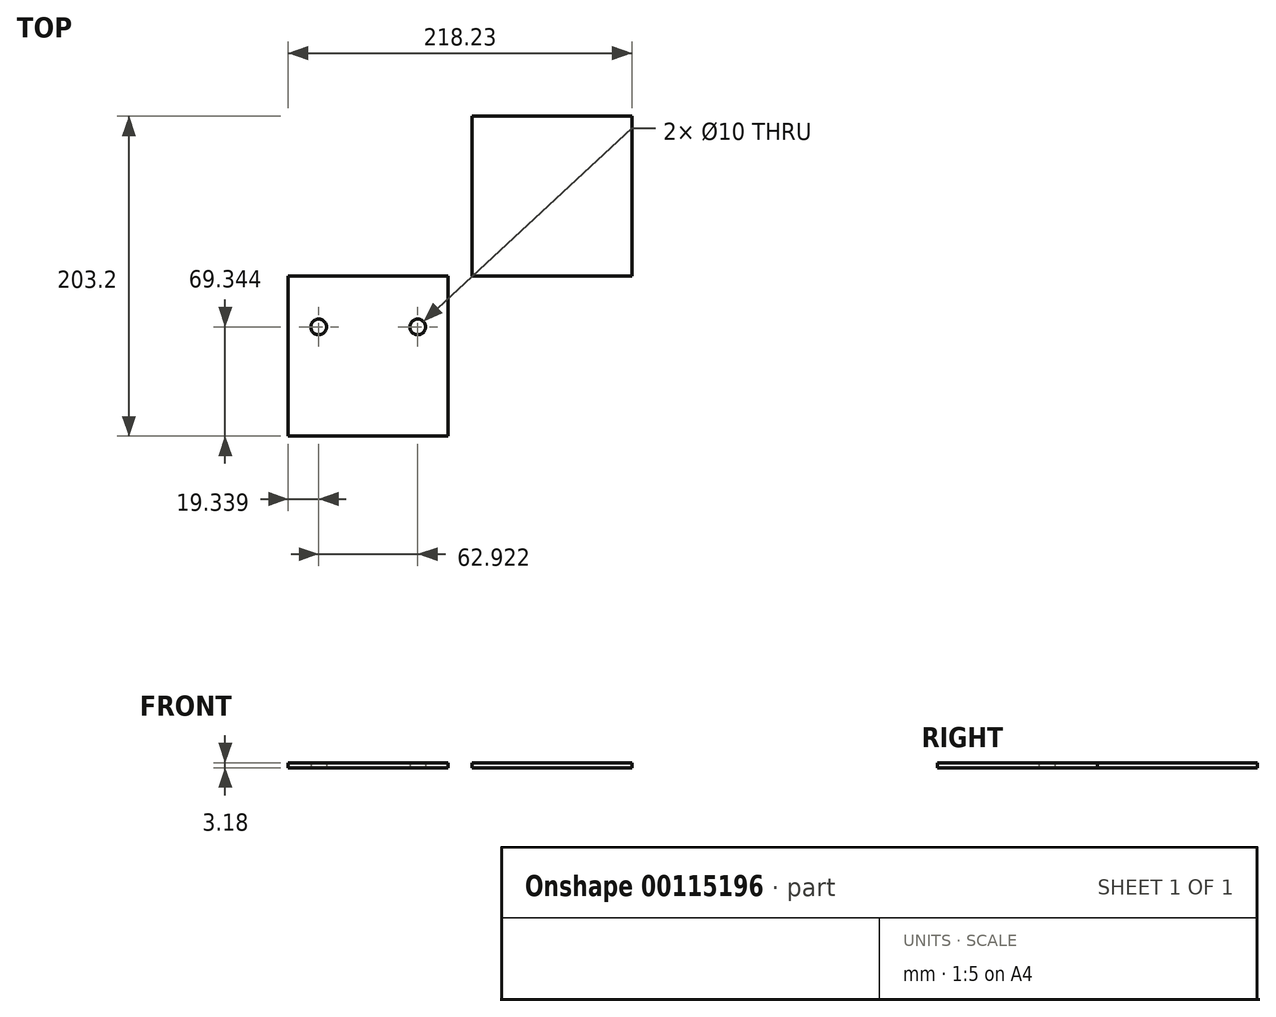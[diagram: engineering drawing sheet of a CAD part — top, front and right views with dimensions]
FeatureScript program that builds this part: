
annotation { "Feature Type Name" : "Feature", "Feature Type Description" : "" }
export const myFeature = defineFeature(function(context is Context, id is Id, definition is map)
    precondition{}
    {
        {
            var Q0;
            Q0=qCreatedBy(makeId("Top.planeOp"),FACE);
            var sketch = newSketch(context, id + "F0", { "sketchPlane" : qUnion([Q0])});
            skLineSegment(sketch, "E0.bottom", {"start": v(-101.6, 0) * mm, "end": v(0, 0) * mm});
            skLineSegment(sketch, "E0.top", {"start": v(-101.6, -101.6) * mm, "end": v(0, -101.6) * mm});
            skLineSegment(sketch, "E0.left", {"start": v(-101.6, 0) * mm, "end": v(-101.6, -101.6) * mm});
            skLineSegment(sketch, "E0.right", {"start": v(0, 0) * mm, "end": v(0, -101.6) * mm});
            skLineSegment(sketch, "E1.bottom", {"start": v(15.03, 0) * mm, "end": v(116.63, 0) * mm});
            skLineSegment(sketch, "E1.top", {"start": v(15.03, 101.6) * mm, "end": v(116.63, 101.6) * mm});
            skLineSegment(sketch, "E1.left", {"start": v(15.03, 0) * mm, "end": v(15.03, 101.6) * mm});
            skLineSegment(sketch, "E1.right", {"start": v(116.63, 0) * mm, "end": v(116.63, 101.6) * mm});
            skCircle(sketch, "E2", {"center": v(-82.26, -32.26) * mm, "radius": 5 * mm});
            skCircle(sketch, "E3.MirrorC", {"center": v(-19.34, -32.26) * mm, "radius": 5 * mm});
            skLineSegment(sketch, "E4", {"start": v(-82.26, -73.7) * mm, "end": v(-20.3, -73.7) * mm});
            skSolve(sketch);
        }
        {
            var Q0;
            Q0=makeQuery(id+"F0.imprint","IMPRINT",FACE,{"disambiguationData":[TD([[makeQuery(id+"F0.imprint","IMPRINT",EDGE,{"derivedFrom":sQuery(id+"F0.wireOp",EDGE,"E0.bottom")}),-1.0]])]});
            extrude(context, id + "F1", {"entities" : qUnion([Q0]), "depth" : 3.17 * mm});
        }
        {
            var Q0;
            Q0=makeQuery(id+"F0.imprint","IMPRINT",FACE,{"disambiguationData":[TD([[makeQuery(id+"F0.imprint","IMPRINT",EDGE,{"derivedFrom":sQuery(id+"F0.wireOp",EDGE,"E1.bottom")}),1.0]])]});
            extrude(context, id + "F2", {"entities" : qUnion([Q0]), "depth" : 3.17 * mm});
        }
    });
